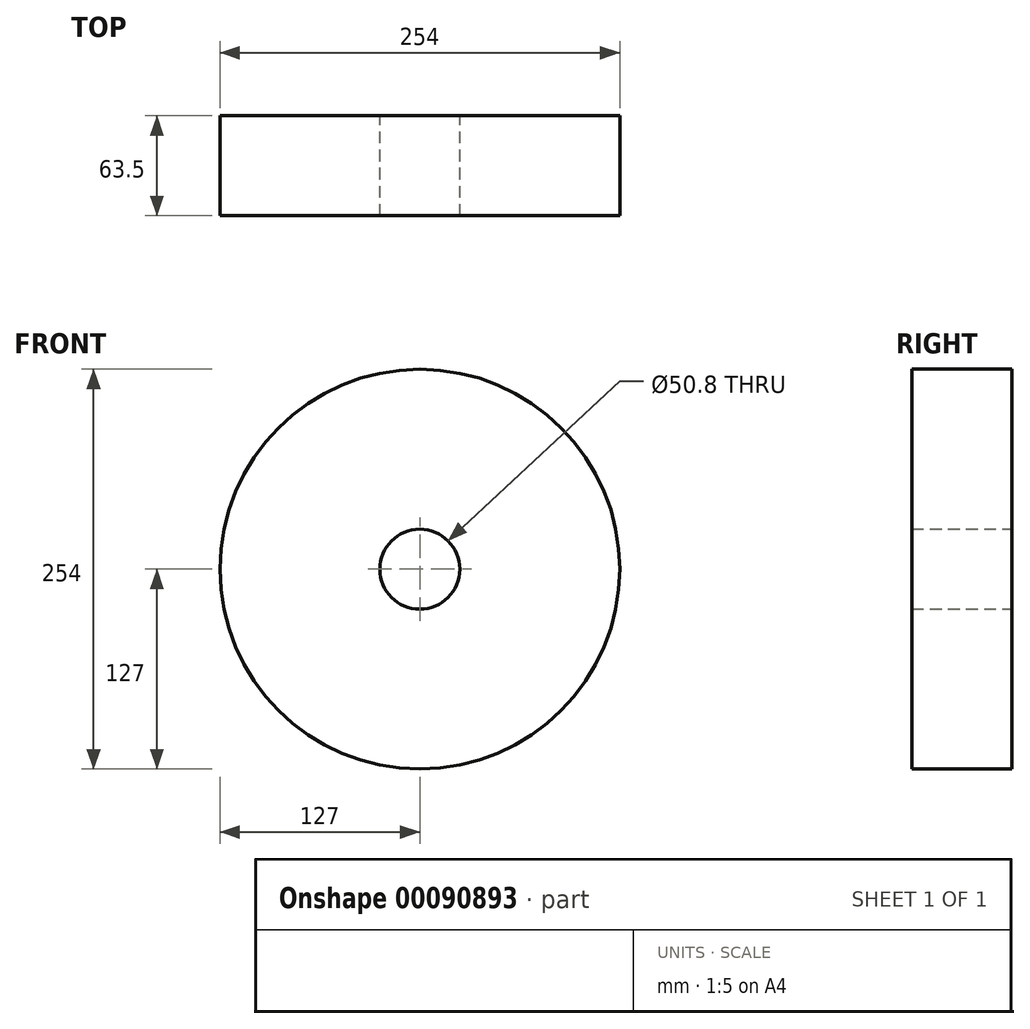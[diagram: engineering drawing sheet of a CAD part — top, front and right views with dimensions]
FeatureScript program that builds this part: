
annotation { "Feature Type Name" : "Feature", "Feature Type Description" : "" }
export const myFeature = defineFeature(function(context is Context, id is Id, definition is map)
    precondition{}
    {
        {
            var Q0;
            Q0=qCreatedBy(makeId("Front.planeOp"),FACE);
            var sketch = newSketch(context, id + "F0", { "sketchPlane" : qUnion([Q0])});
            skCircle(sketch, "E0", {"center": v(0, 0) * mm, "radius": 127 * mm});
            skCircle(sketch, "E1", {"center": v(0, 0) * mm, "radius": 25.4 * mm});
            skSolve(sketch);
        }
        {
            var Q0;
            Q0=makeQuery(id+"F0.imprint","IMPRINT",FACE,{"disambiguationData":[TD([[makeQuery(id+"F0.imprint","IMPRINT",EDGE,{"derivedFrom":sQuery(id+"F0.wireOp",EDGE,"E0")}),1.0]])]});
            extrude(context, id + "F1", {"entities" : qUnion([Q0]), "endBound" : BoundingType.SYMMETRIC, "depth" : 63.5 * mm});
        }
    });
